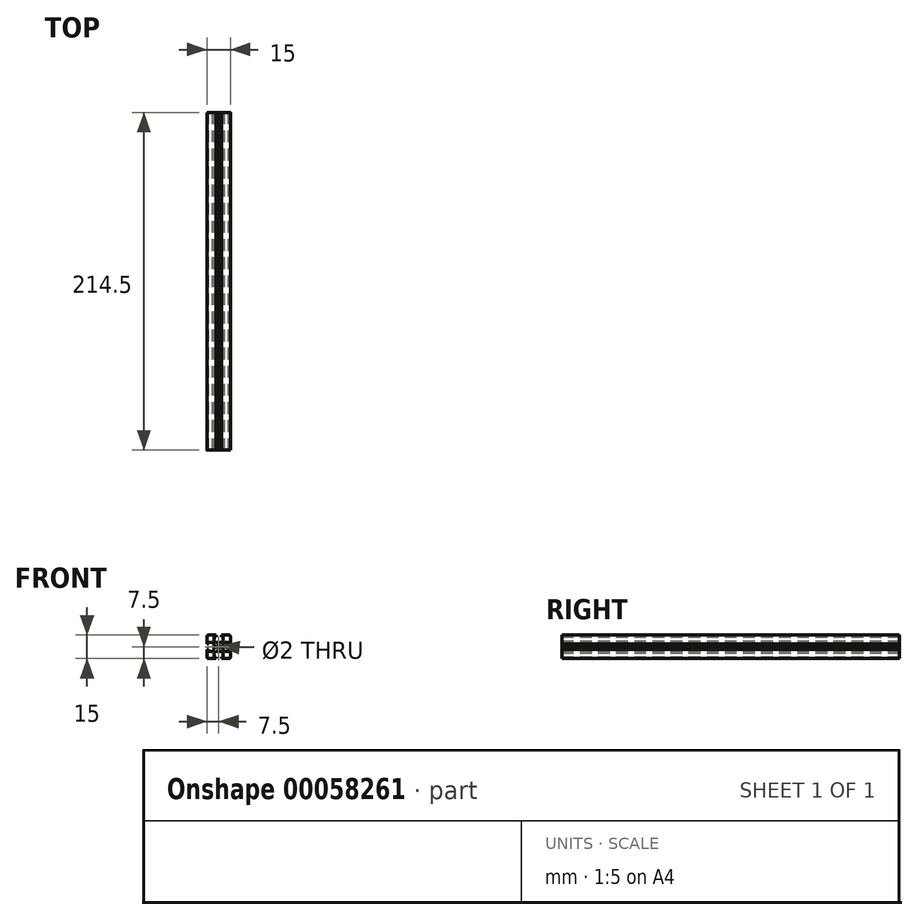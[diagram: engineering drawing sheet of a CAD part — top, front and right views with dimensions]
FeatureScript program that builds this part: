
annotation { "Feature Type Name" : "Feature", "Feature Type Description" : "" }
export const myFeature = defineFeature(function(context is Context, id is Id, definition is map)
    precondition{}
    {
        {
            var Q0;
            Q0=qCreatedBy(makeId("Front.planeOp"),FACE);
            var sketch = newSketch(context, id + "F0", { "sketchPlane" : qUnion([Q0])});
            skCircle(sketch, "E0", {"center": v(0, 0) * mm, "radius": 1 * mm});
            skLineSegment(sketch, "E1.bottom", {"start": v(0, 0) * mm, "end": v(-7.5, 0) * mm, "construction": true});
            skLineSegment(sketch, "E1.top", {"start": v(0, 7.5) * mm, "end": v(-7.5, 7.5) * mm, "construction": true});
            skLineSegment(sketch, "E1.left", {"start": v(0, 0) * mm, "end": v(0, 7.5) * mm, "construction": true});
            skLineSegment(sketch, "E1.right", {"start": v(-7.5, 0) * mm, "end": v(-7.5, 7.5) * mm, "construction": true});
            skLineSegment(sketch, "E2", {"start": v(-2.85, 3.8) * mm, "end": v(-1.7, 2.8) * mm});
            skLineSegment(sketch, "E3", {"start": v(-1.7, 2.8) * mm, "end": v(-0.52, 2.8) * mm});
            skLineSegment(sketch, "E4", {"start": v(-0.52, 2.8) * mm, "end": v(0, 2.5) * mm});
            skLineSegment(sketch, "E5", {"start": v(-7.5, 7.5) * mm, "end": v(-1.7, 7.5) * mm});
            skLineSegment(sketch, "E6", {"start": v(-1.7, 7.5) * mm, "end": v(-1.7, 6.4) * mm});
            skLineSegment(sketch, "E7", {"start": v(-1.7, 6.4) * mm, "end": v(-2.85, 6.4) * mm});
            skLineSegment(sketch, "E8", {"start": v(-2.85, 6.4) * mm, "end": v(-2.85, 3.8) * mm});
            skLineSegment(sketch, "E9", {"start": v(-7.5, 7.5) * mm, "end": v(0, 0) * mm, "construction": true});
            skLineSegment(sketch, "E10.0.MirrorCS", {"start": v(-2.8, 0.52) * mm, "end": v(-2.5, 0) * mm});
            skLineSegment(sketch, "E10.1.MirrorCS", {"start": v(-2.8, 1.7) * mm, "end": v(-2.8, 0.52) * mm});
            skLineSegment(sketch, "E10.2.MirrorCS", {"start": v(-3.8, 2.85) * mm, "end": v(-2.8, 1.7) * mm});
            skLineSegment(sketch, "E10.3.MirrorCS", {"start": v(-6.4, 2.85) * mm, "end": v(-3.8, 2.85) * mm});
            skLineSegment(sketch, "E10.4.MirrorCS", {"start": v(-6.4, 1.7) * mm, "end": v(-6.4, 2.85) * mm});
            skLineSegment(sketch, "E10.5.MirrorCS", {"start": v(-7.5, 1.7) * mm, "end": v(-6.4, 1.7) * mm});
            skLineSegment(sketch, "E10.6.MirrorCS", {"start": v(-7.5, 7.5) * mm, "end": v(-7.5, 1.7) * mm});
            skLineSegment(sketch, "E11.0.MirrorCS", {"start": v(2.8, 0.52) * mm, "end": v(2.5, 0) * mm});
            skLineSegment(sketch, "E11.1.MirrorCS", {"start": v(2.8, 1.7) * mm, "end": v(2.8, 0.52) * mm});
            skLineSegment(sketch, "E11.2.MirrorCS", {"start": v(3.8, 2.85) * mm, "end": v(2.8, 1.7) * mm});
            skLineSegment(sketch, "E11.3.MirrorCS", {"start": v(6.4, 2.85) * mm, "end": v(3.8, 2.85) * mm});
            skLineSegment(sketch, "E11.4.MirrorCS", {"start": v(6.4, 1.7) * mm, "end": v(6.4, 2.85) * mm});
            skLineSegment(sketch, "E11.5.MirrorCS", {"start": v(7.5, 1.7) * mm, "end": v(6.4, 1.7) * mm});
            skLineSegment(sketch, "E11.6.MirrorCS", {"start": v(7.5, 7.5) * mm, "end": v(7.5, 1.7) * mm});
            skLineSegment(sketch, "E11.7.MirrorCS", {"start": v(7.5, 7.5) * mm, "end": v(1.7, 7.5) * mm});
            skLineSegment(sketch, "E11.8.MirrorCS", {"start": v(1.7, 7.5) * mm, "end": v(1.7, 6.4) * mm});
            skLineSegment(sketch, "E11.9.MirrorCS", {"start": v(1.7, 6.4) * mm, "end": v(2.85, 6.4) * mm});
            skLineSegment(sketch, "E11.10.MirrorCS", {"start": v(2.85, 6.4) * mm, "end": v(2.85, 3.8) * mm});
            skLineSegment(sketch, "E11.11.MirrorCS", {"start": v(2.85, 3.8) * mm, "end": v(1.7, 2.8) * mm});
            skLineSegment(sketch, "E11.12.MirrorCS", {"start": v(1.7, 2.8) * mm, "end": v(0.52, 2.8) * mm});
            skLineSegment(sketch, "E11.13.MirrorCS", {"start": v(0.52, 2.8) * mm, "end": v(0, 2.5) * mm});
            skLineSegment(sketch, "E12.0.MirrorCS", {"start": v(2.8, -0.52) * mm, "end": v(2.5, 0) * mm});
            skLineSegment(sketch, "E12.1.MirrorCS", {"start": v(2.8, -1.7) * mm, "end": v(2.8, -0.52) * mm});
            skLineSegment(sketch, "E12.2.MirrorCS", {"start": v(3.8, -2.85) * mm, "end": v(2.8, -1.7) * mm});
            skLineSegment(sketch, "E12.3.MirrorCS", {"start": v(6.4, -2.85) * mm, "end": v(3.8, -2.85) * mm});
            skLineSegment(sketch, "E12.4.MirrorCS", {"start": v(6.4, -1.7) * mm, "end": v(6.4, -2.85) * mm});
            skLineSegment(sketch, "E12.5.MirrorCS", {"start": v(7.5, -1.7) * mm, "end": v(6.4, -1.7) * mm});
            skLineSegment(sketch, "E12.6.MirrorCS", {"start": v(7.5, -7.5) * mm, "end": v(7.5, -1.7) * mm});
            skLineSegment(sketch, "E12.7.MirrorCS", {"start": v(7.5, -7.5) * mm, "end": v(1.7, -7.5) * mm});
            skLineSegment(sketch, "E12.8.MirrorCS", {"start": v(1.7, -7.5) * mm, "end": v(1.7, -6.4) * mm});
            skLineSegment(sketch, "E12.9.MirrorCS", {"start": v(1.7, -6.4) * mm, "end": v(2.85, -6.4) * mm});
            skLineSegment(sketch, "E12.10.MirrorCS", {"start": v(2.85, -6.4) * mm, "end": v(2.85, -3.8) * mm});
            skLineSegment(sketch, "E12.11.MirrorCS", {"start": v(2.85, -3.8) * mm, "end": v(1.7, -2.8) * mm});
            skLineSegment(sketch, "E12.12.MirrorCS", {"start": v(1.7, -2.8) * mm, "end": v(0.52, -2.8) * mm});
            skLineSegment(sketch, "E12.13.MirrorCS", {"start": v(0.52, -2.8) * mm, "end": v(0, -2.5) * mm});
            skLineSegment(sketch, "E12.14.MirrorCS", {"start": v(-0.52, -2.8) * mm, "end": v(0, -2.5) * mm});
            skLineSegment(sketch, "E12.15.MirrorCS", {"start": v(-1.7, -2.8) * mm, "end": v(-0.52, -2.8) * mm});
            skLineSegment(sketch, "E12.16.MirrorCS", {"start": v(-2.85, -3.8) * mm, "end": v(-1.7, -2.8) * mm});
            skLineSegment(sketch, "E12.17.MirrorCS", {"start": v(-2.85, -6.4) * mm, "end": v(-2.85, -3.8) * mm});
            skLineSegment(sketch, "E12.18.MirrorCS", {"start": v(-1.7, -6.4) * mm, "end": v(-2.85, -6.4) * mm});
            skLineSegment(sketch, "E12.19.MirrorCS", {"start": v(-1.7, -7.5) * mm, "end": v(-1.7, -6.4) * mm});
            skLineSegment(sketch, "E12.20.MirrorCS", {"start": v(-7.5, -7.5) * mm, "end": v(-1.7, -7.5) * mm});
            skLineSegment(sketch, "E12.21.MirrorCS", {"start": v(-7.5, -7.5) * mm, "end": v(-7.5, -1.7) * mm});
            skLineSegment(sketch, "E12.22.MirrorCS", {"start": v(-7.5, -1.7) * mm, "end": v(-6.4, -1.7) * mm});
            skLineSegment(sketch, "E12.23.MirrorCS", {"start": v(-6.4, -1.7) * mm, "end": v(-6.4, -2.85) * mm});
            skLineSegment(sketch, "E12.24.MirrorCS", {"start": v(-6.4, -2.85) * mm, "end": v(-3.8, -2.85) * mm});
            skLineSegment(sketch, "E12.25.MirrorCS", {"start": v(-3.8, -2.85) * mm, "end": v(-2.8, -1.7) * mm});
            skLineSegment(sketch, "E12.26.MirrorCS", {"start": v(-2.8, -1.7) * mm, "end": v(-2.8, -0.52) * mm});
            skLineSegment(sketch, "E12.27.MirrorCS", {"start": v(-2.8, -0.52) * mm, "end": v(-2.5, 0) * mm});
            skSolve(sketch);
        }
        {
            var Q0;
            Q0=qSketchRegion(id+"F0",true);
            extrude(context, id + "F1", {"entities" : qUnion([Q0]), "depth" : (429 / 2) * mm, "symmetric" : true});
        }
        {
            var Q0;
            Q0=makeQuery(id+"F1.opExtrude","SWEPT_EDGE",EDGE,{"disambiguationData":[OSD([sQuery(id+"F0.wireOp",EDGE,"E11.6.MirrorCS"),sQuery(id+"F0.wireOp",EDGE,"E11.7.MirrorCS")])]});
            var Q1;
            Q1=makeQuery(id+"F1.opExtrude","SWEPT_EDGE",EDGE,{"disambiguationData":[OSD([sQuery(id+"F0.wireOp",EDGE,"E5"),sQuery(id+"F0.wireOp",EDGE,"E10.6.MirrorCS")])]});
            var Q2;
            Q2=makeQuery(id+"F1.opExtrude","SWEPT_EDGE",EDGE,{"disambiguationData":[OSD([sQuery(id+"F0.wireOp",EDGE,"E12.6.MirrorCS"),sQuery(id+"F0.wireOp",EDGE,"E12.7.MirrorCS")])]});
            var Q3;
            Q3=makeQuery(id+"F1.opExtrude","SWEPT_EDGE",EDGE,{"disambiguationData":[OSD([sQuery(id+"F0.wireOp",EDGE,"E12.20.MirrorCS"),sQuery(id+"F0.wireOp",EDGE,"E12.21.MirrorCS")])]});
            fillet(context, id + "F2", {"entities" : qUnion([Q0, Q1, Q2, Q3]), "radius" : 1.1 * mm, "tangentPropagation" : true, "allowEdgeOverflow" : false});
        }
    });
